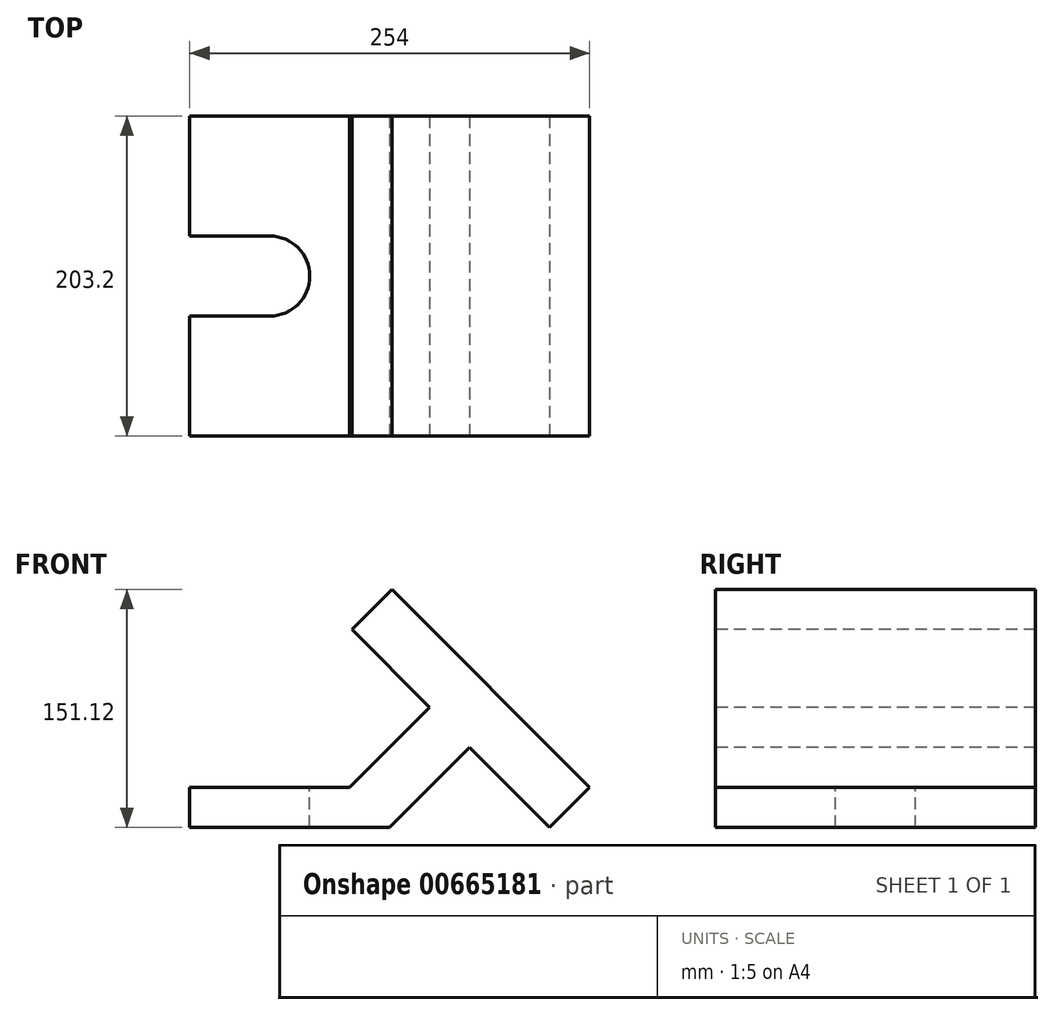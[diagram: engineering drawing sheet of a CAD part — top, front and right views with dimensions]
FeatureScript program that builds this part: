
annotation { "Feature Type Name" : "Feature", "Feature Type Description" : "" }
export const myFeature = defineFeature(function(context is Context, id is Id, definition is map)
    precondition{}
    {
        {
            var Q0;
            Q0=qCreatedBy(makeId("Front.planeOp"),FACE);
            var sketch = newSketch(context, id + "F0", { "sketchPlane" : qUnion([Q0])});
            skLineSegment(sketch, "E0", {"start": v(0, 0) * mm, "end": v(127, 0) * mm});
            skLineSegment(sketch, "E1", {"start": v(127, 0) * mm, "end": v(177.8, 50.8) * mm});
            skLineSegment(sketch, "E2", {"start": v(177.8, 50.8) * mm, "end": v(228.6, 0) * mm});
            skLineSegment(sketch, "E3", {"start": v(228.6, 0) * mm, "end": v(254, 25.4) * mm});
            skLineSegment(sketch, "E4", {"start": v(254, 25.4) * mm, "end": v(128.28, 151.12) * mm});
            skLineSegment(sketch, "E5", {"start": v(128.28, 151.12) * mm, "end": v(102.88, 125.72) * mm});
            skLineSegment(sketch, "E6", {"start": v(102.88, 125.72) * mm, "end": v(152.4, 76.2) * mm});
            skLineSegment(sketch, "E7", {"start": v(152.4, 76.2) * mm, "end": v(101.6, 25.4) * mm});
            skLineSegment(sketch, "E8", {"start": v(101.6, 25.4) * mm, "end": v(0, 25.4) * mm});
            skLineSegment(sketch, "E9", {"start": v(0, 25.4) * mm, "end": v(0, 0) * mm});
            skLineSegment(sketch, "E10", {"start": v(127, 0) * mm, "end": v(228.6, 0) * mm, "construction": true});
            skSolve(sketch);
        }
        {
            var Q0;
            Q0=makeQuery(id+"F0.imprint","IMPRINT",FACE,{"disambiguationData":[TD([[makeQuery(id+"F0.imprint","IMPRINT",EDGE,{"derivedFrom":sQuery(id+"F0.wireOp",EDGE,"E0")}),1.0]])]});
            extrude(context, id + "F1", {"entities" : qUnion([Q0]), "oppositeDirection" : true, "depth" : 203.2 * mm, "offsetDistance" : 25.4 * mm});
        }
        {
            var Q0;
            Q0=makeQuery(id+"F1.opExtrude","SWEPT_FACE",FACE,{"disambiguationData":[OSD([sQuery(id+"F0.wireOp",EDGE,"E8")])]});
            var sketch = newSketch(context, id + "F2", { "sketchPlane" : qUnion([Q0])});
            skArc(sketch, "E11", {"start": v(50.8, 76.2) * mm, "mid": v(76.2, 101.6) * mm, "end": v(50.8, 127) * mm});
            skLineSegment(sketch, "E12", {"start": v(0, 127) * mm, "end": v(50.8, 127) * mm});
            skLineSegment(sketch, "E13", {"start": v(0, 76.2) * mm, "end": v(50.8, 76.2) * mm});
            skLineSegment(sketch, "E14", {"start": v(0, 76.2) * mm, "end": v(0, 127) * mm});
            skSolve(sketch);
        }
        {
            var Q0;
            Q0=makeQuery(id+"F2.imprint","IMPRINT",FACE,{"disambiguationData":[TD([[makeQuery(id+"F2.imprint","IMPRINT",EDGE,{"derivedFrom":sQuery(id+"F2.wireOp",EDGE,"E11")}),1.0]])]});
            extrude(context, id + "F3", {"entities" : qUnion([Q0]), "operationType" : NewBodyOperationType.REMOVE, "oppositeDirection" : true, "depth" : 38.1 * mm, "offsetDistance" : 25.4 * mm});
        }
        {
            var Q0;
            Q0=makeQuery(id+"F1.opExtrude","SWEPT_FACE",FACE,{"disambiguationData":[OSD([sQuery(id+"F0.wireOp",EDGE,"E4")])]});
            var sketch = newSketch(context, id + "F4", { "sketchPlane" : qUnion([Q0])});
            skArc(sketch, "E15", {"start": v(-3.46, 50.8) * mm, "mid": v(21.94, 25.4) * mm, "end": v(47.34, 50.8) * mm});
            skArc(sketch, "E16", {"start": v(47.34, 152.4) * mm, "mid": v(21.94, 177.8) * mm, "end": v(-3.46, 152.4) * mm});
            skArc(sketch, "E17", {"start": v(98.14, 50.8) * mm, "mid": v(123.54, 25.4) * mm, "end": v(148.94, 50.8) * mm});
            skArc(sketch, "E18", {"start": v(148.94, 152.4) * mm, "mid": v(123.54, 177.8) * mm, "end": v(98.14, 152.4) * mm});
            skLineSegment(sketch, "E19", {"start": v(-3.46, 50.8) * mm, "end": v(-3.46, 152.4) * mm});
            skLineSegment(sketch, "E20", {"start": v(47.34, 50.8) * mm, "end": v(47.34, 152.4) * mm});
            skLineSegment(sketch, "E21", {"start": v(98.14, 50.8) * mm, "end": v(98.14, 152.4) * mm});
            skLineSegment(sketch, "E22", {"start": v(148.94, 50.8) * mm, "end": v(148.94, 152.4) * mm});
            skSolve(sketch);
        }
        {
            var Q0;
            Q0=makeQuery(id+"F4.imprint","IMPRINT",FACE,{"disambiguationData":[TD([[makeQuery(id+"F4.imprint","IMPRINT",EDGE,{"derivedFrom":sQuery(id+"F4.wireOp",EDGE,"E15")}),1.0]])]});
            var Q1;
            Q1=makeQuery(id+"F4.imprint","IMPRINT",FACE,{"disambiguationData":[TD([[makeQuery(id+"F4.imprint","IMPRINT",EDGE,{"derivedFrom":sQuery(id+"F4.wireOp",EDGE,"E17")}),1.0]])]});
            extrude(context, id + "F5", {"entities" : qUnion([Q0, Q1]), "operationType" : NewBodyOperationType.REMOVE, "oppositeDirection" : true, "depth" : 50.8 * mm, "offsetDistance" : 25.4 * mm});
        }
    });
